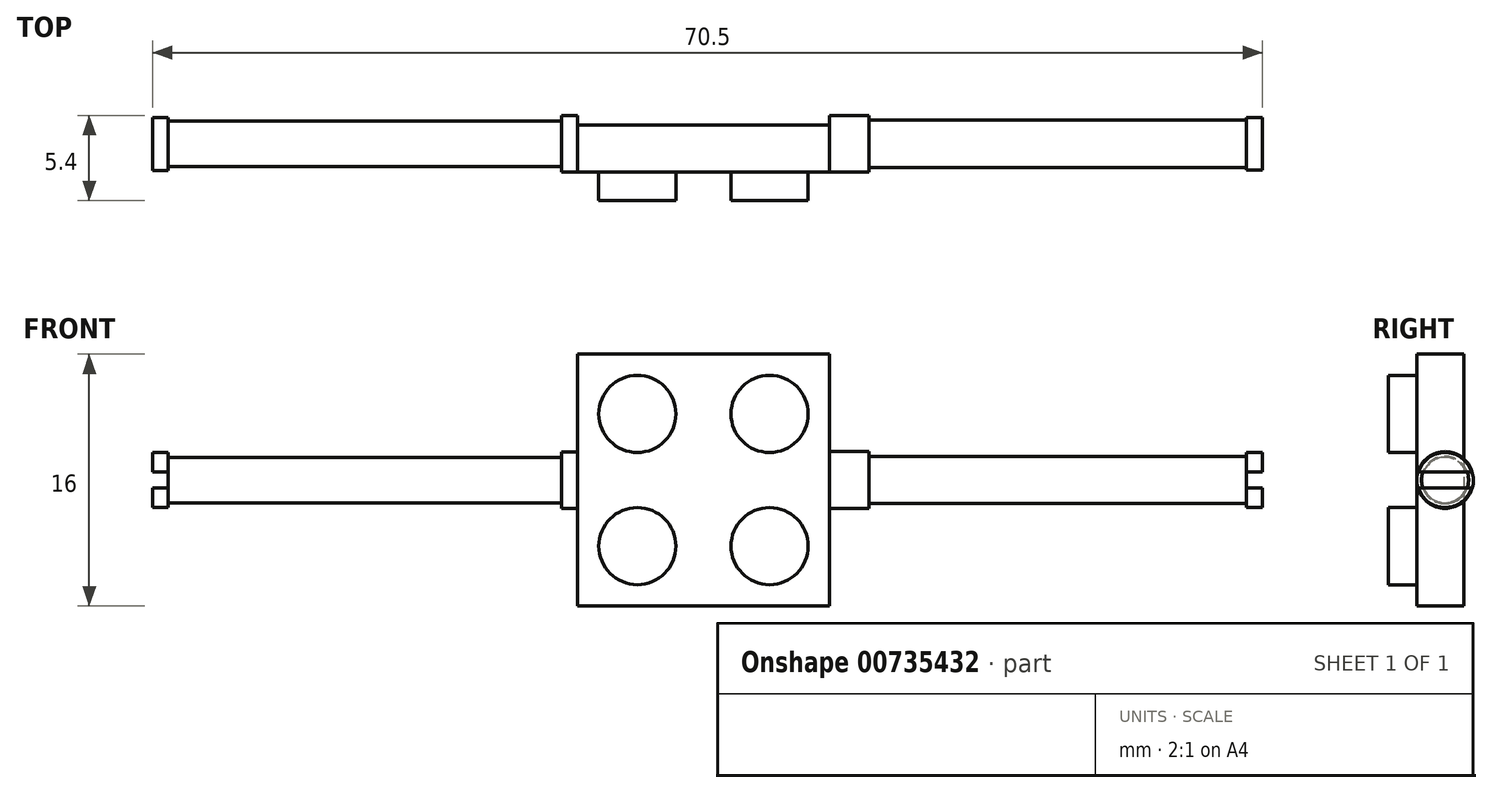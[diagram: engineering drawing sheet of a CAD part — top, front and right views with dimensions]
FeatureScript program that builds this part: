
annotation { "Feature Type Name" : "Feature", "Feature Type Description" : "" }
export const myFeature = defineFeature(function(context is Context, id is Id, definition is map)
    precondition{}
    {
        {
            var Q0;
            Q0=qCreatedBy(makeId("Front.planeOp"),FACE);
            var sketch = newSketch(context, id + "F0", { "sketchPlane" : qUnion([Q0])});
            skLineSegment(sketch, "E0.bottom", {"start": v(-8, 8) * mm, "end": v(8, 8) * mm});
            skLineSegment(sketch, "E0.top", {"start": v(-8, -8) * mm, "end": v(8, -8) * mm});
            skLineSegment(sketch, "E0.left", {"start": v(-8, 8) * mm, "end": v(-8, -8) * mm});
            skLineSegment(sketch, "E0.right", {"start": v(8, 8) * mm, "end": v(8, -8) * mm});
            skPoint(sketch, "E0.middle", {"position": v(0, 0) * mm});
            skPoint(sketch, "E1.center.orphan", {"position": v(-4.2, 4.2) * mm});
            skPoint(sketch, "E2.center.orphan", {"position": v(4.2, 4.2) * mm});
            skPoint(sketch, "E3.center.orphan", {"position": v(-4.2, -4.2) * mm});
            skPoint(sketch, "E4.center.orphan", {"position": v(4.2, -4.2) * mm});
            skSolve(sketch);
        }
        {
            var Q0;
            Q0 = qSketchRegion(id + "F0", true);
            extrude(context, id + "F1", {"entities" : qUnion([Q0]), "depth" : 3 * mm, "offsetDistance" : 25 * mm});
        }
        {
            var Q0;
            Q0=makeQuery(id+"F1.opExtrude","CAP_FACE",FACE,{"disambiguationData":[OSD([sQuery(id+"F0.wireOp",EDGE,"E0.bottom"),sQuery(id+"F0.wireOp",EDGE,"E0.top"),sQuery(id+"F0.wireOp",EDGE,"E0.left"),sQuery(id+"F0.wireOp",EDGE,"E0.right")])],"isStart":false});
            var sketch = newSketch(context, id + "F2", { "sketchPlane" : qUnion([Q0])});
            skCircle(sketch, "E5", {"center": v(-4.2, 4.2) * mm, "radius": 2.45 * mm});
            skCircle(sketch, "E6", {"center": v(4.2, 4.2) * mm, "radius": 2.45 * mm});
            skCircle(sketch, "E7", {"center": v(-4.2, -4.2) * mm, "radius": 2.45 * mm});
            skCircle(sketch, "E8", {"center": v(4.2, -4.2) * mm, "radius": 2.45 * mm});
            skSolve(sketch);
        }
        {
            var Q0;
            Q0 = qSketchRegion(id + "F2", true);
            extrude(context, id + "F3", {"entities" : qUnion([Q0]), "operationType" : NewBodyOperationType.ADD, "depth" : 1.8 * mm, "offsetDistance" : 25 * mm});
        }
        {
            var Q0;
            Q0=makeQuery(id+"F1.opExtrude","SWEPT_FACE",FACE,{"disambiguationData":[OSD([sQuery(id+"F0.wireOp",EDGE,"E0.right")])]});
            var sketch = newSketch(context, id + "F4", { "sketchPlane" : qUnion([Q0])});
            skCircle(sketch, "E9", {"center": v(-1.2, 0) * mm, "radius": 1.8 * mm});
            skSolve(sketch);
        }
        {
            var Q0;
            Q0 = qSketchRegion(id + "F4", true);
            extrude(context, id + "F5", {"entities" : qUnion([Q0]), "operationType" : NewBodyOperationType.ADD, "depth" : 2.5 * mm, "offsetDistance" : 25 * mm});
        }
        {
            var Q0;
            Q0=makeQuery(id+"F5.opExtrude","CAP_FACE",FACE,{"disambiguationData":[OSD([sQuery(id+"F4.wireOp",EDGE,"E9")])],"isStart":false});
            var sketch = newSketch(context, id + "F6", { "sketchPlane" : qUnion([Q0])});
            skCircle(sketch, "E10", {"center": v(-1.2, 0) * mm, "radius": 1.5 * mm});
            skSolve(sketch);
        }
        {
            var Q0;
            Q0 = qSketchRegion(id + "F6", true);
            extrude(context, id + "F7", {"entities" : qUnion([Q0]), "operationType" : NewBodyOperationType.ADD, "depth" : 25 * mm, "offsetDistance" : 25 * mm});
        }
        {
            var Q0;
            Q0=makeQuery(id+"F7.opExtrude","CAP_FACE",FACE,{"disambiguationData":[OSD([sQuery(id+"F6.wireOp",EDGE,"E10")])],"isStart":false});
            var sketch = newSketch(context, id + "F8", { "sketchPlane" : qUnion([Q0])});
            skCircle(sketch, "E11", {"center": v(-1.2, 0) * mm, "radius": 1.75 * mm});
            skSolve(sketch);
        }
        {
            var Q0;
            Q0 = qSketchRegion(id + "F8", true);
            extrude(context, id + "F9", {"entities" : qUnion([Q0]), "operationType" : NewBodyOperationType.ADD, "oppositeDirection" : true, "depth" : 1 * mm, "offsetDistance" : 25 * mm});
        }
        {
            var Q0;
            Q0=makeQuery(id+"F9.boolean.opBoolean","MERGE",FACE,{"derivedFrom":[makeQuery(id+"F7.opExtrude","CAP_FACE",FACE,{"disambiguationData":[OSD([sQuery(id+"F6.wireOp",EDGE,"E10")])],"isStart":false}),makeQuery(id+"F9.opExtrude","CAP_FACE",FACE,{"disambiguationData":[OSD([sQuery(id+"F8.wireOp",EDGE,"E11")])],"isStart":true})]});
            var sketch = newSketch(context, id + "F10", { "sketchPlane" : qUnion([Q0])});
            skLineSegment(sketch, "E12", {"start": v(-2.88, 0.5) * mm, "end": v(0.48, 0.5) * mm});
            skLineSegment(sketch, "E13", {"start": v(0.48, -0.5) * mm, "end": v(-2.88, -0.5) * mm});
            skSolve(sketch);
        }
        {
            var Q0;
            Q0 = qSketchRegion(id + "F10", true);
            var Q1;
            {var subQ0=sQuery(id+"F10.wireOp",EDGE,"E12");Q1=makeQuery(id+"F10.imprint","IMPRINT",FACE,{"disambiguationData":[TD([[makeQuery(id+"F10.imprint","IMPRINT",EDGE,{"derivedFrom":subQ0}),-1.0]])]});}
            extrude(context, id + "F11", {"entities" : qUnion([Q0, Q1]), "operationType" : NewBodyOperationType.REMOVE, "oppositeDirection" : true, "depth" : 1 * mm, "offsetDistance" : 25 * mm});
        }
        {
            var Q0;
            Q0=makeQuery(id+"F1.opExtrude","SWEPT_FACE",FACE,{"disambiguationData":[OSD([sQuery(id+"F0.wireOp",EDGE,"E0.left")])]});
            var sketch = newSketch(context, id + "F12", { "sketchPlane" : qUnion([Q0])});
            skLineSegment(sketch, "E14", {"start": v(3, 0) * mm, "end": v(-0.6, 0) * mm});
            skCircle(sketch, "E15", {"center": v(1.2, 0) * mm, "radius": 1.8 * mm});
            skSolve(sketch);
        }
        {
            var Q0;
            Q0 = qSketchRegion(id + "F12", true);
            extrude(context, id + "F13", {"entities" : qUnion([Q0]), "operationType" : NewBodyOperationType.ADD, "depth" : 1 * mm, "offsetDistance" : 25 * mm});
        }
        {
            var Q0;
            Q0=makeQuery(id+"F13.opExtrude","CAP_FACE",FACE,{"disambiguationData":[OSD([sQuery(id+"F12.wireOp",EDGE,"E15")])],"isStart":false});
            var sketch = newSketch(context, id + "F14", { "sketchPlane" : qUnion([Q0])});
            skCircle(sketch, "E16", {"center": v(1.2, 0) * mm, "radius": 1.45 * mm});
            skSolve(sketch);
        }
        {
            var Q0;
            Q0 = qSketchRegion(id + "F14", true);
            extrude(context, id + "F15", {"entities" : qUnion([Q0]), "operationType" : NewBodyOperationType.ADD, "depth" : 25 * mm, "offsetDistance" : 25 * mm});
        }
        {
            var Q0;
            Q0=makeQuery(id+"F15.opExtrude","CAP_FACE",FACE,{"disambiguationData":[OSD([sQuery(id+"F14.wireOp",EDGE,"E16")])],"isStart":false});
            var sketch = newSketch(context, id + "F16", { "sketchPlane" : qUnion([Q0])});
            skCircle(sketch, "E17", {"center": v(1.2, 0) * mm, "radius": 1.75 * mm});
            skSolve(sketch);
        }
        {
            var Q0;
            Q0 = qSketchRegion(id + "F16", true);
            extrude(context, id + "F17", {"entities" : qUnion([Q0]), "operationType" : NewBodyOperationType.ADD, "depth" : 1 * mm, "offsetDistance" : 25 * mm});
        }
        {
            var Q0;
            Q0=makeQuery(id+"F17.opExtrude","CAP_FACE",FACE,{"disambiguationData":[OSD([sQuery(id+"F16.wireOp",EDGE,"E17")])],"isStart":false});
            var sketch = newSketch(context, id + "F18", { "sketchPlane" : qUnion([Q0])});
            skLineSegment(sketch, "E18", {"start": v(-0.47, 0.5) * mm, "end": v(2.88, 0.5) * mm});
            skLineSegment(sketch, "E19", {"start": v(2.88, -0.5) * mm, "end": v(-0.47, -0.5) * mm});
            skSolve(sketch);
        }
        {
            var Q0;
            {var subQ0=sQuery(id+"F18.wireOp",EDGE,"E18");Q0=makeQuery(id+"F18.imprint","IMPRINT",FACE,{"disambiguationData":[TD([[makeQuery(id+"F18.imprint","IMPRINT",EDGE,{"derivedFrom":subQ0}),-1.0]])]});}
            extrude(context, id + "F19", {"entities" : qUnion([Q0]), "operationType" : NewBodyOperationType.REMOVE, "oppositeDirection" : true, "depth" : 1 * mm, "offsetDistance" : 25 * mm});
        }
    });
